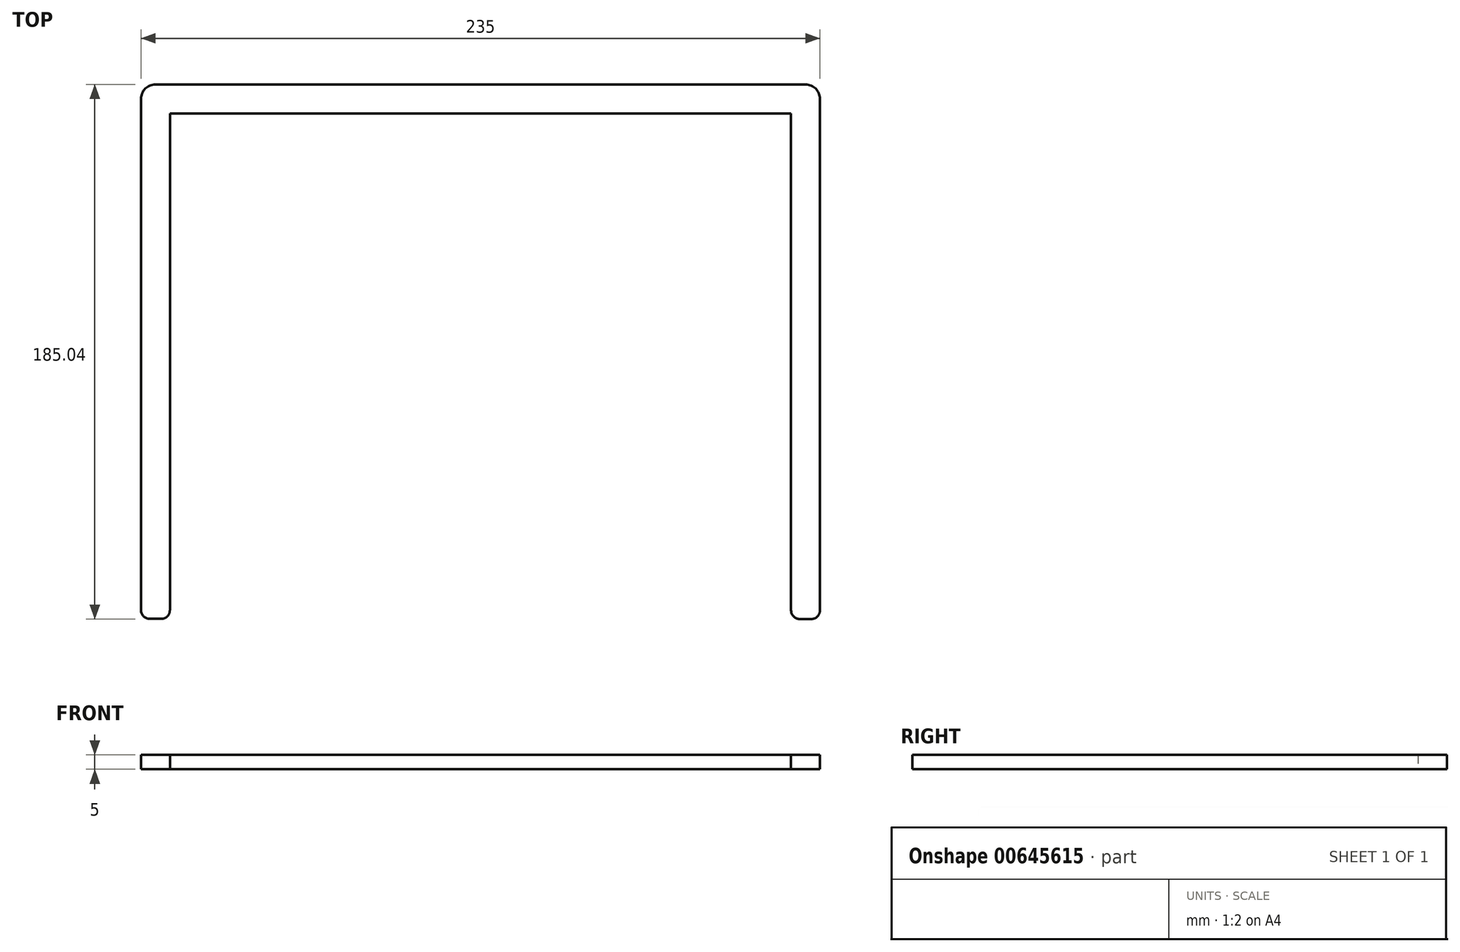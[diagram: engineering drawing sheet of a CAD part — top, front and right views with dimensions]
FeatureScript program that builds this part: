
annotation { "Feature Type Name" : "Feature", "Feature Type Description" : "" }
export const myFeature = defineFeature(function(context is Context, id is Id, definition is map)
    precondition{}
    {
        {
            var Q0;
            Q0=qCreatedBy(makeId("Top.planeOp"),FACE);
            var sketch = newSketch(context, id + "F0", { "sketchPlane" : qUnion([Q0])});
            skLineSegment(sketch, "E0.top", {"start": v(107.5, 87.5) * mm, "end": v(-107.5, 87.5) * mm});
            skLineSegment(sketch, "E0.left", {"start": v(107.5, -84.52) * mm, "end": v(107.5, 87.5) * mm});
            skLineSegment(sketch, "E0.right", {"start": v(-107.5, -84.48) * mm, "end": v(-107.5, 87.5) * mm});
            skPoint(sketch, "E0.middle", {"position": v(0, 0) * mm});
            skLineSegment(sketch, "E1.0", {"start": v(112.5, 97.5) * mm, "end": v(-112.5, 97.5) * mm});
            skLineSegment(sketch, "E2.0", {"start": v(117.5, -84.54) * mm, "end": v(117.5, 92.5) * mm});
            skLineSegment(sketch, "E3.0", {"start": v(-117.5, -84.46) * mm, "end": v(-117.5, 92.5) * mm});
            skLineSegment(sketch, "E4", {"start": v(-114.52, -87.46) * mm, "end": v(-110.52, -87.48) * mm});
            skLineSegment(sketch, "E5", {"start": v(110.48, -87.52) * mm, "end": v(114.48, -87.54) * mm});
            skPoint(sketch, "E6.visualSharp", {"position": v(-117.5, 97.5) * mm});
            skArc(sketch, "E6.filletArc", {"start": v(-112.5, 97.5) * mm, "mid": v(-116.04, 96.04) * mm, "end": v(-117.5, 92.5) * mm});
            skPoint(sketch, "E7.visualSharp", {"position": v(117.5, 97.5) * mm});
            skArc(sketch, "E7.filletArc", {"start": v(117.5, 92.5) * mm, "mid": v(116.04, 96.04) * mm, "end": v(112.5, 97.5) * mm});
            skPoint(sketch, "E8.visualSharp", {"position": v(107.5, -87.5) * mm});
            skArc(sketch, "E8.filletArc", {"start": v(107.5, -84.52) * mm, "mid": v(108.37, -86.63) * mm, "end": v(110.48, -87.52) * mm});
            skPoint(sketch, "E9.visualSharp", {"position": v(117.5, -87.55) * mm});
            skArc(sketch, "E9.filletArc", {"start": v(114.48, -87.54) * mm, "mid": v(116.62, -86.67) * mm, "end": v(117.5, -84.54) * mm});
            skPoint(sketch, "E10.visualSharp", {"position": v(-107.5, -87.5) * mm});
            skArc(sketch, "E10.filletArc", {"start": v(-110.52, -87.48) * mm, "mid": v(-108.38, -86.61) * mm, "end": v(-107.5, -84.48) * mm});
            skPoint(sketch, "E11.visualSharp", {"position": v(-117.5, -87.45) * mm});
            skArc(sketch, "E11.filletArc", {"start": v(-117.5, -84.46) * mm, "mid": v(-116.63, -86.58) * mm, "end": v(-114.52, -87.46) * mm});
            skSolve(sketch);
        }
        {
            var Q0;
            Q0 = qSketchRegion(id + "F0", true);
            extrude(context, id + "F1", {"entities" : qUnion([Q0]), "depth" : 5 * mm, "offsetDistance" : 25 * mm});
        }
    });
